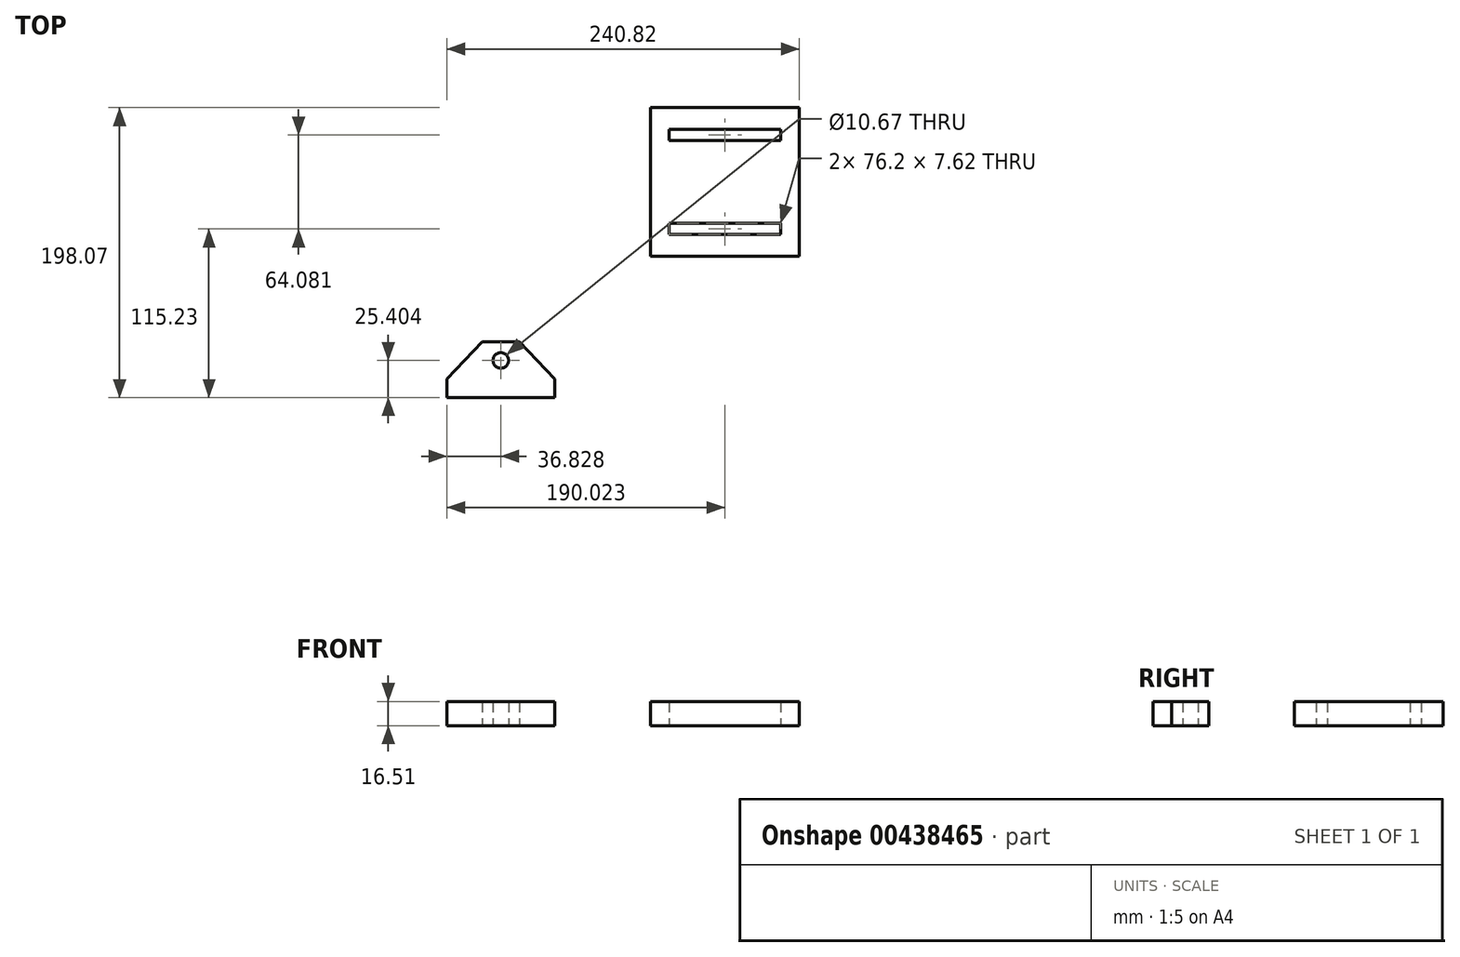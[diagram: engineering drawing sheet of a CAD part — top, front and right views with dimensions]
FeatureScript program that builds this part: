
annotation { "Feature Type Name" : "Feature", "Feature Type Description" : "" }
export const myFeature = defineFeature(function(context is Context, id is Id, definition is map)
    precondition{}
    {
        {
            var Q0;
            Q0=qCreatedBy(makeId("Top.planeOp"),FACE);
            var sketch = newSketch(context, id + "F0", { "sketchPlane" : qUnion([Q0])});
            skLineSegment(sketch, "E0.bottom", {"start": v(-62.14, 174.8) * mm, "end": v(39.46, 174.8) * mm});
            skLineSegment(sketch, "E0.top", {"start": v(-62.14, 73.2) * mm, "end": v(39.46, 73.2) * mm});
            skLineSegment(sketch, "E0.left", {"start": v(-62.14, 174.8) * mm, "end": v(-62.14, 73.2) * mm});
            skLineSegment(sketch, "E0.right", {"start": v(39.46, 174.8) * mm, "end": v(39.46, 73.2) * mm});
            skLineSegment(sketch, "E1.bottom", {"start": v(-49.44, 159.84) * mm, "end": v(26.76, 159.84) * mm});
            skLineSegment(sketch, "E1.top", {"start": v(-49.44, 152.22) * mm, "end": v(26.76, 152.22) * mm});
            skLineSegment(sketch, "E1.left", {"start": v(-49.44, 159.84) * mm, "end": v(-49.44, 152.22) * mm});
            skLineSegment(sketch, "E1.right", {"start": v(26.76, 159.84) * mm, "end": v(26.76, 152.22) * mm});
            skLineSegment(sketch, "E2", {"start": v(-62.14, 124) * mm, "end": v(39.46, 124) * mm, "construction": true});
            skLineSegment(sketch, "E3.MirrorCS", {"start": v(-49.44, 88.14) * mm, "end": v(26.76, 88.14) * mm});
            skLineSegment(sketch, "E4.MirrorCS", {"start": v(-49.44, 95.76) * mm, "end": v(26.76, 95.76) * mm});
            skLineSegment(sketch, "E5.MirrorCS", {"start": v(26.76, 88.14) * mm, "end": v(26.76, 95.76) * mm});
            skLineSegment(sketch, "E6.MirrorCS", {"start": v(-49.44, 88.14) * mm, "end": v(-49.44, 95.76) * mm});
            skSolve(sketch);
        }
        {
            var Q0;
            Q0=makeQuery(id+"F0.imprint","IMPRINT",FACE,{"disambiguationData":[TD([[makeQuery(id+"F0.imprint","IMPRINT",EDGE,{"derivedFrom":sQuery(id+"F0.wireOp",EDGE,"E0.bottom")}),-1.0]])]});
            extrude(context, id + "F1", {"entities" : qUnion([Q0]), "depth" : 16.5 * mm});
        }
        {
            var Q0;
            Q0=qCreatedBy(makeId("Top.planeOp"),FACE);
            var sketch = newSketch(context, id + "F2", { "sketchPlane" : qUnion([Q0])});
            skLineSegment(sketch, "E7.bottom", {"start": v(-201.36, -10.58) * mm, "end": v(-127.7, -10.58) * mm, "construction": true});
            skLineSegment(sketch, "E7.top", {"start": v(-201.36, -23.28) * mm, "end": v(-127.7, -23.28) * mm});
            skLineSegment(sketch, "E7.left", {"start": v(-201.36, -10.58) * mm, "end": v(-201.36, -23.28) * mm});
            skLineSegment(sketch, "E7.right", {"start": v(-127.7, -10.58) * mm, "end": v(-127.7, -23.28) * mm});
            skLineSegment(sketch, "E8", {"start": v(-164.53, -10.58) * mm, "end": v(-164.53, 14.82) * mm, "construction": true});
            skLineSegment(sketch, "E9", {"start": v(-164.53, 14.82) * mm, "end": v(-151.83, 14.82) * mm});
            skLineSegment(sketch, "E10", {"start": v(-164.53, 14.82) * mm, "end": v(-177.23, 14.82) * mm});
            skLineSegment(sketch, "E11", {"start": v(-177.23, 14.82) * mm, "end": v(-201.36, -10.58) * mm});
            skLineSegment(sketch, "E12", {"start": v(-151.83, 14.82) * mm, "end": v(-127.7, -10.58) * mm});
            skCircle(sketch, "E13", {"center": v(-164.53, 2.12) * mm, "radius": 5.33 * mm});
            skSolve(sketch);
        }
        {
            var Q0;
            Q0=makeQuery(id+"F2.imprint","IMPRINT",FACE,{"disambiguationData":[TD([[makeQuery(id+"F2.imprint","IMPRINT",EDGE,{"derivedFrom":sQuery(id+"F2.wireOp",EDGE,"E7.top")}),1.0]])]});
            extrude(context, id + "F3", {"entities" : qUnion([Q0]), "depth" : 16.5 * mm});
        }
    });
